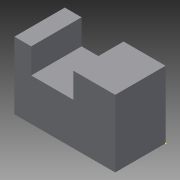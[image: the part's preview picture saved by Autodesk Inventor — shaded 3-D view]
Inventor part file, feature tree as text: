
AUTODESK INVENTOR PART (.ipt)
format: ipt  version: 2015 (Build 190159000, 159)  size: 77,824 bytes
history: native  units: in
note: dims shown in document units (in); Inventor stores cm internally (conversion verified against a paired STEP export)
features: sketch x2, extrude x1
ambient origin geometry x8: Origin, YZ Plane, XZ Plane, XY Plane, X Axis, Y Axis, Z Axis, Center Point
bodies: Solid1 (feature_tree)
feature tree (3):
  extrude  "Extrusion1"  Depth=60.0in
  sketch  "Sketch2"  dims[d2=40.0in d3=15.0in d4=10.0in d5=25.0in d6=30.0in d7=0.0in]
  sketch  "Sketch1"  dims[d0=40.0in d1=60.0in]
